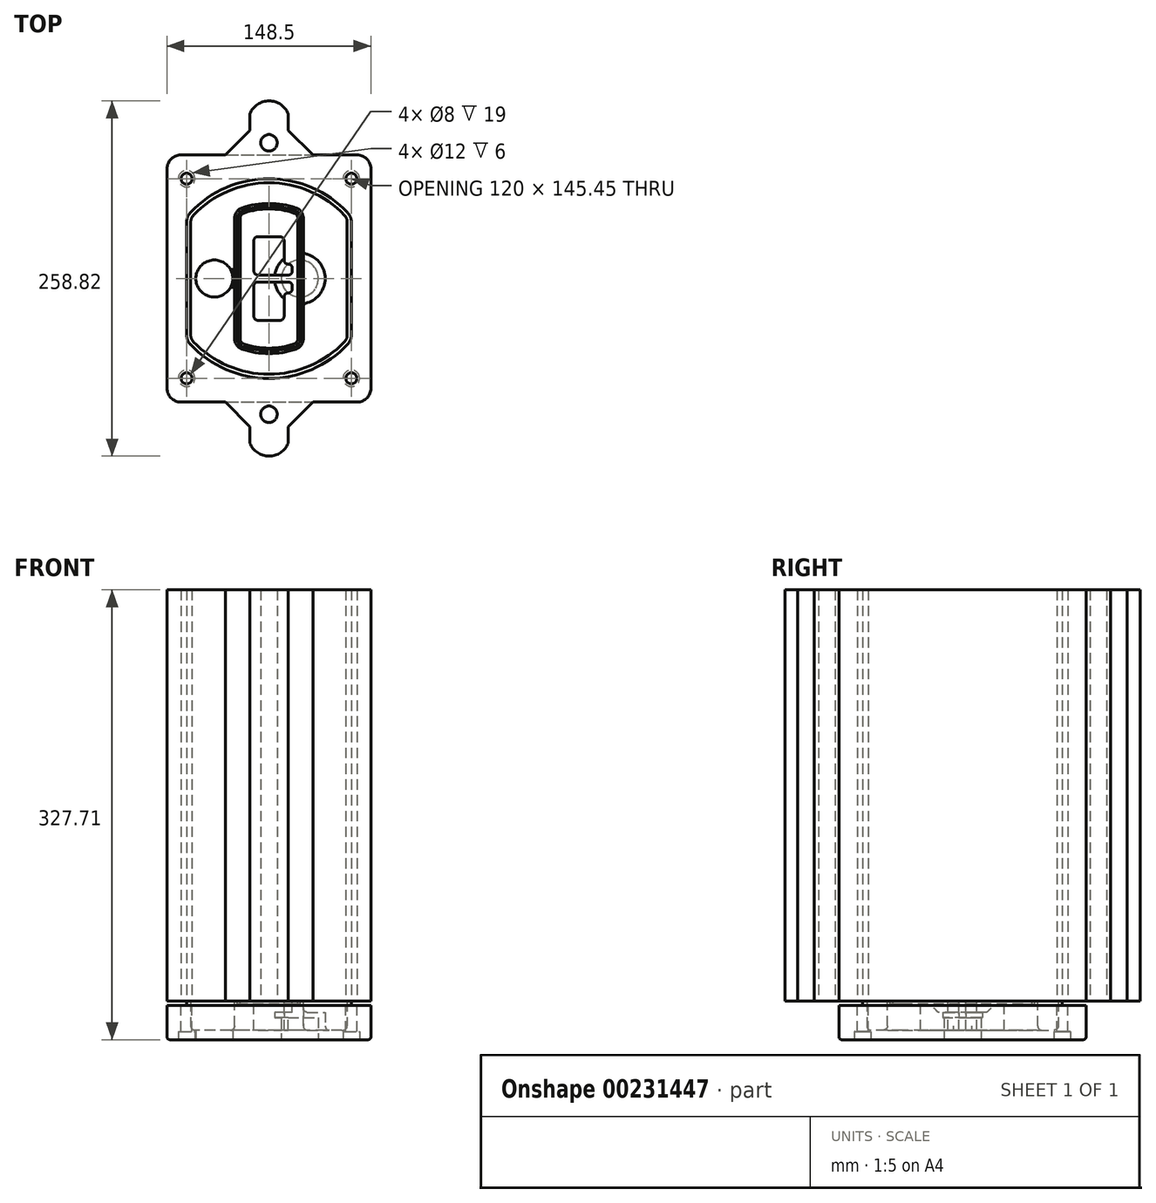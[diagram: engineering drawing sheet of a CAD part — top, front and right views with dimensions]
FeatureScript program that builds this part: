
annotation { "Feature Type Name" : "Feature", "Feature Type Description" : "" }
export const myFeature = defineFeature(function(context is Context, id is Id, definition is map)
    precondition{}
    {
        {
            var Q0;
            Q0=qCreatedBy(makeId("Top.planeOp"),FACE);
            var sketch = newSketch(context, id + "F0", { "sketchPlane" : qUnion([Q0])});
            skPoint(sketch, "E0.rect.middle", {"position": v(0, 0) * mm});
            skLineSegment(sketch, "E1.bottom", {"start": v(-64.25, -90) * mm, "end": v(64.25, -90) * mm});
            skLineSegment(sketch, "E1.top", {"start": v(-64.25, 90) * mm, "end": v(64.25, 90) * mm});
            skLineSegment(sketch, "E1.left", {"start": v(-74.25, -80) * mm, "end": v(-74.25, 80) * mm});
            skLineSegment(sketch, "E1.right", {"start": v(74.25, -80) * mm, "end": v(74.25, 80) * mm});
            skLineSegment(sketch, "E2", {"start": v(-74.25, 90) * mm, "end": v(74.25, -90) * mm, "construction": true});
            skLineSegment(sketch, "E3", {"start": v(74.25, 90) * mm, "end": v(-74.25, -90) * mm, "construction": true});
            skCircle(sketch, "E4", {"center": v(-60, 72.73) * mm, "radius": 4 * mm});
            skCircle(sketch, "E5", {"center": v(60, 72.73) * mm, "radius": 4 * mm});
            skCircle(sketch, "E6", {"center": v(60, -72.73) * mm, "radius": 4 * mm});
            skCircle(sketch, "E7", {"center": v(-60, -72.73) * mm, "radius": 4 * mm});
            skLineSegment(sketch, "E8", {"start": v(-60, 72.73) * mm, "end": v(60, 72.73) * mm, "construction": true});
            skLineSegment(sketch, "E9", {"start": v(60, 72.73) * mm, "end": v(60, -72.73) * mm, "construction": true});
            skLineSegment(sketch, "E10", {"start": v(60, -72.73) * mm, "end": v(-60, -72.73) * mm, "construction": true});
            skLineSegment(sketch, "E11", {"start": v(-60, -72.73) * mm, "end": v(-60, 72.73) * mm, "construction": true});
            skLineSegment(sketch, "E12", {"start": v(-60, 41.18) * mm, "end": v(-60, -41.18) * mm});
            skLineSegment(sketch, "E13", {"start": v(60, 41.18) * mm, "end": v(60, -41.18) * mm});
            skArc(sketch, "E14", {"start": v(57.27, 48.05) * mm, "mid": v(0, 72.73) * mm, "end": v(-57.27, 48.05) * mm});
            skArc(sketch, "E15", {"start": v(-57.27, -48.05) * mm, "mid": v(0, -72.73) * mm, "end": v(57.27, -48.05) * mm});
            skLineSegment(sketch, "E16", {"start": v(-60, 0) * mm, "end": v(60, 0) * mm, "construction": true});
            skPoint(sketch, "E17.visualSharp", {"position": v(-60, -45) * mm});
            skArc(sketch, "E17.filletArc", {"start": v(-60, -41.18) * mm, "mid": v(-59.3, -44.87) * mm, "end": v(-57.27, -48.05) * mm});
            skPoint(sketch, "E18.visualSharp", {"position": v(-60, 45) * mm});
            skArc(sketch, "E18.filletArc", {"start": v(-57.27, 48.05) * mm, "mid": v(-59.3, 44.87) * mm, "end": v(-60, 41.18) * mm});
            skPoint(sketch, "E19.visualSharp", {"position": v(60, 45) * mm});
            skArc(sketch, "E19.filletArc", {"start": v(60, 41.18) * mm, "mid": v(59.3, 44.87) * mm, "end": v(57.27, 48.05) * mm});
            skPoint(sketch, "E20.visualSharp", {"position": v(60, -45) * mm});
            skArc(sketch, "E20.filletArc", {"start": v(57.27, -48.05) * mm, "mid": v(59.3, -44.87) * mm, "end": v(60, -41.18) * mm});
            skPoint(sketch, "E21.visualSharp", {"position": v(-74.25, 90) * mm});
            skArc(sketch, "E21.filletArc", {"start": v(-64.25, 90) * mm, "mid": v(-71.32, 87.07) * mm, "end": v(-74.25, 80) * mm});
            skPoint(sketch, "E22.visualSharp", {"position": v(74.25, 90) * mm});
            skArc(sketch, "E22.filletArc", {"start": v(74.25, 80) * mm, "mid": v(71.32, 87.07) * mm, "end": v(64.25, 90) * mm});
            skPoint(sketch, "E23.visualSharp", {"position": v(74.25, -90) * mm});
            skArc(sketch, "E23.filletArc", {"start": v(64.25, -90) * mm, "mid": v(71.32, -87.07) * mm, "end": v(74.25, -80) * mm});
            skPoint(sketch, "E24.visualSharp", {"position": v(-74.25, -90) * mm});
            skArc(sketch, "E24.filletArc", {"start": v(-74.25, -80) * mm, "mid": v(-71.32, -87.07) * mm, "end": v(-64.25, -90) * mm});
            skArc(sketch, "E25.0", {"start": v(57, 41.18) * mm, "mid": v(56.5, 43.76) * mm, "end": v(55.09, 45.99) * mm});
            skLineSegment(sketch, "E25.1", {"start": v(57, 41.18) * mm, "end": v(57, -41.18) * mm});
            skArc(sketch, "E25.2", {"start": v(55.09, -45.99) * mm, "mid": v(56.5, -43.76) * mm, "end": v(57, -41.18) * mm});
            skArc(sketch, "E25.3", {"start": v(-55.09, -45.99) * mm, "mid": v(0, -69.73) * mm, "end": v(55.09, -45.99) * mm});
            skArc(sketch, "E25.4", {"start": v(-57, -41.18) * mm, "mid": v(-56.5, -43.76) * mm, "end": v(-55.09, -45.99) * mm});
            skArc(sketch, "E25.5", {"start": v(55.09, 45.99) * mm, "mid": v(0, 69.73) * mm, "end": v(-55.09, 45.99) * mm});
            skLineSegment(sketch, "E25.6", {"start": v(-57, 41.18) * mm, "end": v(-57, -41.18) * mm});
            skArc(sketch, "E25.7", {"start": v(-55.09, 45.99) * mm, "mid": v(-56.5, 43.76) * mm, "end": v(-57, 41.18) * mm});
            skArc(sketch, "E26.0", {"start": v(-60.18, 50.8) * mm, "mid": v(-63, 46.35) * mm, "end": v(-64, 41.18) * mm});
            skArc(sketch, "E26.1", {"start": v(60.18, 50.8) * mm, "mid": v(0, 76.73) * mm, "end": v(-60.18, 50.8) * mm});
            skArc(sketch, "E26.2", {"start": v(64, 41.18) * mm, "mid": v(63, 46.35) * mm, "end": v(60.18, 50.8) * mm});
            skLineSegment(sketch, "E26.3", {"start": v(64, 41.18) * mm, "end": v(64, -41.18) * mm});
            skArc(sketch, "E26.4", {"start": v(60.18, -50.8) * mm, "mid": v(63, -46.35) * mm, "end": v(64, -41.18) * mm});
            skLineSegment(sketch, "E26.5", {"start": v(-64, 41.18) * mm, "end": v(-64, -41.18) * mm});
            skArc(sketch, "E26.6", {"start": v(-60.18, -50.8) * mm, "mid": v(0, -76.73) * mm, "end": v(60.18, -50.8) * mm});
            skArc(sketch, "E26.7", {"start": v(-64, -41.18) * mm, "mid": v(-63, -46.35) * mm, "end": v(-60.18, -50.8) * mm});
            skSolve(sketch);
        }
        {
            var Q0;
            Q0=makeQuery(id+"F0.imprint","IMPRINT",FACE,{"disambiguationData":[TD([[makeQuery(id+"F0.imprint","IMPRINT",EDGE,{"derivedFrom":sQuery(id+"F0.wireOp",EDGE,"E1.bottom")}),1.0]])]});
            var Q1;
            Q1=makeQuery(id+"F0.imprint","IMPRINT",FACE,{"disambiguationData":[TD([[makeQuery(id+"F0.imprint","IMPRINT",EDGE,{"derivedFrom":sQuery(id+"F0.wireOp",EDGE,"E12")}),1.0]])]});
            var Q2;
            Q2=makeQuery(id+"F0.imprint","IMPRINT",FACE,{"disambiguationData":[TD([[makeQuery(id+"F0.imprint","IMPRINT",EDGE,{"derivedFrom":sQuery(id+"F0.wireOp",EDGE,"E25.0")}),1.0]])]});
            var Q3;
            Q3=makeQuery(id+"F0.imprint","IMPRINT",FACE,{"disambiguationData":[TD([[makeQuery(id+"F0.imprint","IMPRINT",EDGE,{"derivedFrom":sQuery(id+"F0.wireOp",EDGE,"E12")}),-1.0]])]});
            extrude(context, id + "F1", {"entities" : qUnion([Q0, Q1, Q2, Q3]), "oppositeDirection" : true, "depth" : 25 * mm});
        }
        {
            var Q0;
            Q0=makeQuery(id+"F0.imprint","IMPRINT",FACE,{"disambiguationData":[TD([[makeQuery(id+"F0.imprint","IMPRINT",EDGE,{"derivedFrom":sQuery(id+"F0.wireOp",EDGE,"E12")}),1.0]])]});
            extrude(context, id + "F2", {"entities" : qUnion([Q0]), "operationType" : NewBodyOperationType.ADD, "depth" : 3 * mm});
        }
        {
            var Q0;
            Q0=makeQuery(id+"F0.imprint","IMPRINT",FACE,{"disambiguationData":[TD([[makeQuery(id+"F0.imprint","IMPRINT",EDGE,{"derivedFrom":sQuery(id+"F0.wireOp",EDGE,"E25.0")}),1.0]])]});
            extrude(context, id + "F3", {"entities" : qUnion([Q0]), "operationType" : NewBodyOperationType.REMOVE, "oppositeDirection" : true, "depth" : 18 * mm});
        }
        {
            var Q0;
            Q0=makeQuery(id+"F2.opExtrude","CAP_FACE",FACE,{"disambiguationData":[OSD([sQuery(id+"F0.wireOp",EDGE,"E12"),sQuery(id+"F0.wireOp",EDGE,"E13"),sQuery(id+"F0.wireOp",EDGE,"E14"),sQuery(id+"F0.wireOp",EDGE,"E15"),sQuery(id+"F0.wireOp",EDGE,"E17.filletArc"),sQuery(id+"F0.wireOp",EDGE,"E18.filletArc"),sQuery(id+"F0.wireOp",EDGE,"E19.filletArc"),sQuery(id+"F0.wireOp",EDGE,"E20.filletArc"),sQuery(id+"F0.wireOp",EDGE,"E25.0"),sQuery(id+"F0.wireOp",EDGE,"E25.1"),sQuery(id+"F0.wireOp",EDGE,"E25.2"),sQuery(id+"F0.wireOp",EDGE,"E25.3"),sQuery(id+"F0.wireOp",EDGE,"E25.4"),sQuery(id+"F0.wireOp",EDGE,"E25.5"),sQuery(id+"F0.wireOp",EDGE,"E25.6"),sQuery(id+"F0.wireOp",EDGE,"E25.7")])],"isStart":false});
            var sketch = newSketch(context, id + "F4", { "sketchPlane" : qUnion([Q0])});
            skArc(sketch, "E27.0", {"start": v(-19.58, -51.49) * mm, "mid": v(0, -54.73) * mm, "end": v(19.58, -51.49) * mm});
            skArc(sketch, "E28.0", {"start": v(19.58, 51.49) * mm, "mid": v(0, 54.73) * mm, "end": v(-19.58, 51.49) * mm});
            skLineSegment(sketch, "E29", {"start": v(-25, 43.91) * mm, "end": v(-25, -43.91) * mm});
            skLineSegment(sketch, "E30", {"start": v(25, 43.91) * mm, "end": v(25, -43.91) * mm});
            skLineSegment(sketch, "E31", {"start": v(-25, 49.35) * mm, "end": v(25, 49.35) * mm, "construction": true});
            skLineSegment(sketch, "E32", {"start": v(-25, -49.35) * mm, "end": v(25, -49.35) * mm, "construction": true});
            skPoint(sketch, "E33.visualSharp", {"position": v(-25, 49.35) * mm});
            skArc(sketch, "E33.filletArc", {"start": v(-19.58, 51.49) * mm, "mid": v(-23.5, 48.57) * mm, "end": v(-25, 43.91) * mm});
            skPoint(sketch, "E34.visualSharp", {"position": v(25, 49.35) * mm});
            skArc(sketch, "E34.filletArc", {"start": v(25, 43.91) * mm, "mid": v(23.5, 48.57) * mm, "end": v(19.58, 51.49) * mm});
            skPoint(sketch, "E35.visualSharp", {"position": v(25, -49.35) * mm});
            skArc(sketch, "E35.filletArc", {"start": v(19.58, -51.49) * mm, "mid": v(23.5, -48.57) * mm, "end": v(25, -43.91) * mm});
            skPoint(sketch, "E36.visualSharp", {"position": v(-25, -49.35) * mm});
            skArc(sketch, "E36.filletArc", {"start": v(-25, -43.91) * mm, "mid": v(-23.5, -48.57) * mm, "end": v(-19.58, -51.49) * mm});
            skArc(sketch, "E37.0", {"start": v(55.09, 45.99) * mm, "mid": v(0, 69.73) * mm, "end": v(-55.09, 45.99) * mm});
            skArc(sketch, "E37.1", {"start": v(-55.09, 45.99) * mm, "mid": v(-56.5, 43.76) * mm, "end": v(-57, 41.18) * mm});
            skLineSegment(sketch, "E37.2", {"start": v(-57, 41.18) * mm, "end": v(-57, -41.18) * mm});
            skArc(sketch, "E37.3", {"start": v(-57, -41.18) * mm, "mid": v(-56.5, -43.76) * mm, "end": v(-55.09, -45.99) * mm});
            skArc(sketch, "E37.4", {"start": v(-55.09, -45.99) * mm, "mid": v(0, -69.73) * mm, "end": v(55.09, -45.99) * mm});
            skArc(sketch, "E37.5", {"start": v(55.09, -45.99) * mm, "mid": v(56.5, -43.76) * mm, "end": v(57, -41.18) * mm});
            skLineSegment(sketch, "E37.6", {"start": v(57, 41.18) * mm, "end": v(57, -41.18) * mm});
            skArc(sketch, "E37.7", {"start": v(57, 41.18) * mm, "mid": v(56.5, 43.76) * mm, "end": v(55.09, 45.99) * mm});
            skLineSegment(sketch, "E38.0", {"start": v(23, 43.91) * mm, "end": v(23, -43.91) * mm});
            skArc(sketch, "E38.1", {"start": v(18.93, -49.6) * mm, "mid": v(21.88, -47.4) * mm, "end": v(23, -43.91) * mm});
            skArc(sketch, "E38.2", {"start": v(-18.93, -49.6) * mm, "mid": v(0, -52.73) * mm, "end": v(18.93, -49.6) * mm});
            skArc(sketch, "E38.3", {"start": v(-23, -43.91) * mm, "mid": v(-21.88, -47.4) * mm, "end": v(-18.93, -49.6) * mm});
            skLineSegment(sketch, "E38.4", {"start": v(-23, 43.91) * mm, "end": v(-23, -43.91) * mm});
            skArc(sketch, "E38.5", {"start": v(23, 43.91) * mm, "mid": v(21.88, 47.4) * mm, "end": v(18.93, 49.6) * mm});
            skArc(sketch, "E38.6", {"start": v(-18.93, 49.6) * mm, "mid": v(-21.88, 47.4) * mm, "end": v(-23, 43.91) * mm});
            skArc(sketch, "E38.7", {"start": v(18.93, 49.6) * mm, "mid": v(0, 52.73) * mm, "end": v(-18.93, 49.6) * mm});
            skArc(sketch, "E39.0", {"start": v(21, 43.91) * mm, "mid": v(20.25, 46.24) * mm, "end": v(18.29, 47.7) * mm});
            skLineSegment(sketch, "E39.1", {"start": v(21, 43.91) * mm, "end": v(21, -43.91) * mm});
            skArc(sketch, "E39.2", {"start": v(18.29, -47.7) * mm, "mid": v(20.25, -46.24) * mm, "end": v(21, -43.91) * mm});
            skArc(sketch, "E39.3", {"start": v(-18.29, -47.7) * mm, "mid": v(0, -50.73) * mm, "end": v(18.29, -47.7) * mm});
            skArc(sketch, "E39.4", {"start": v(-21, -43.91) * mm, "mid": v(-20.25, -46.24) * mm, "end": v(-18.29, -47.7) * mm});
            skArc(sketch, "E39.5", {"start": v(18.29, 47.7) * mm, "mid": v(0, 50.73) * mm, "end": v(-18.29, 47.7) * mm});
            skLineSegment(sketch, "E39.6", {"start": v(-21, 43.91) * mm, "end": v(-21, -43.91) * mm});
            skArc(sketch, "E39.7", {"start": v(-18.29, 47.7) * mm, "mid": v(-20.25, 46.24) * mm, "end": v(-21, 43.91) * mm});
            skLineSegment(sketch, "E40", {"start": v(-25, 0) * mm, "end": v(25, 0) * mm, "construction": true});
            skLineSegment(sketch, "E41", {"start": v(-11, 5.5) * mm, "end": v(-11, 27.5) * mm});
            skLineSegment(sketch, "E42", {"start": v(-8, 30.5) * mm, "end": v(8, 30.5) * mm});
            skLineSegment(sketch, "E43", {"start": v(11, 27.5) * mm, "end": v(11, 13.5) * mm});
            skLineSegment(sketch, "E44", {"start": v(14, 10.5) * mm, "end": v(14, 10.5) * mm});
            skLineSegment(sketch, "E45", {"start": v(17, 7.5) * mm, "end": v(17, 5.5) * mm});
            skLineSegment(sketch, "E46", {"start": v(14, 2.5) * mm, "end": v(-8, 2.5) * mm});
            skPoint(sketch, "E47.visualSharp", {"position": v(-11, 30.5) * mm});
            skArc(sketch, "E47.filletArc", {"start": v(-8, 30.5) * mm, "mid": v(-10.12, 29.62) * mm, "end": v(-11, 27.5) * mm});
            skPoint(sketch, "E48.visualSharp", {"position": v(11, 30.5) * mm});
            skArc(sketch, "E48.filletArc", {"start": v(11, 27.5) * mm, "mid": v(10.12, 29.62) * mm, "end": v(8, 30.5) * mm});
            skPoint(sketch, "E49.visualSharp", {"position": v(11, 10.5) * mm});
            skArc(sketch, "E49.filletArc", {"start": v(11, 13.5) * mm, "mid": v(11.88, 11.38) * mm, "end": v(14, 10.5) * mm});
            skPoint(sketch, "E50.visualSharp", {"position": v(17, 10.5) * mm});
            skArc(sketch, "E50.filletArc", {"start": v(17, 7.5) * mm, "mid": v(16.12, 9.62) * mm, "end": v(14, 10.5) * mm});
            skPoint(sketch, "E51.visualSharp", {"position": v(17, 2.5) * mm});
            skArc(sketch, "E51.filletArc", {"start": v(14, 2.5) * mm, "mid": v(16.12, 3.38) * mm, "end": v(17, 5.5) * mm});
            skPoint(sketch, "E52.visualSharp", {"position": v(-11, 2.5) * mm});
            skArc(sketch, "E52.filletArc", {"start": v(-11, 5.5) * mm, "mid": v(-10.12, 3.38) * mm, "end": v(-8, 2.5) * mm});
            skLineSegment(sketch, "E53.0.MirrorCS", {"start": v(14, -2.5) * mm, "end": v(-8, -2.5) * mm});
            skArc(sketch, "E54.0.MirrorCS", {"start": v(-11, -5.5) * mm, "mid": v(-10.12, -3.38) * mm, "end": v(-8, -2.5) * mm});
            skLineSegment(sketch, "E55.0.MirrorCS", {"start": v(-11, -5.5) * mm, "end": v(-11, -27.5) * mm});
            skArc(sketch, "E56.0.MirrorCS", {"start": v(-8, -30.5) * mm, "mid": v(-10.12, -29.62) * mm, "end": v(-11, -27.5) * mm});
            skLineSegment(sketch, "E57.0.MirrorCS", {"start": v(-8, -30.5) * mm, "end": v(8, -30.5) * mm});
            skArc(sketch, "E58.0.MirrorCS", {"start": v(11, -27.5) * mm, "mid": v(10.12, -29.62) * mm, "end": v(8, -30.5) * mm});
            skLineSegment(sketch, "E59.0.MirrorCS", {"start": v(11, -27.5) * mm, "end": v(11, -13.5) * mm});
            skArc(sketch, "E60.0.MirrorCS", {"start": v(11, -13.5) * mm, "mid": v(11.88, -11.38) * mm, "end": v(14, -10.5) * mm});
            skArc(sketch, "E61.0.MirrorCS", {"start": v(17, -7.5) * mm, "mid": v(16.12, -9.62) * mm, "end": v(14, -10.5) * mm});
            skLineSegment(sketch, "E62.0.MirrorCS", {"start": v(17, -7.5) * mm, "end": v(17, -5.5) * mm});
            skArc(sketch, "E63.0.MirrorCS", {"start": v(14, -2.5) * mm, "mid": v(16.12, -3.38) * mm, "end": v(17, -5.5) * mm});
            skSolve(sketch);
        }
        {
            var Q0;
            Q0=makeQuery(id+"F4.imprint","IMPRINT",FACE,{"disambiguationData":[TD([[makeQuery(id+"F4.imprint","IMPRINT",EDGE,{"derivedFrom":sQuery(id+"F4.wireOp",EDGE,"E27.0")}),1.0]])]});
            var Q1;
            Q1=makeQuery(id+"F4.imprint","IMPRINT",FACE,{"disambiguationData":[TD([[makeQuery(id+"F4.imprint","IMPRINT",EDGE,{"derivedFrom":sQuery(id+"F4.wireOp",EDGE,"E38.0")}),-1.0]])]});
            var Q2;
            Q2=makeQuery(id+"F4.imprint","IMPRINT",FACE,{"disambiguationData":[TD([[makeQuery(id+"F4.imprint","IMPRINT",EDGE,{"derivedFrom":sQuery(id+"F4.wireOp",EDGE,"E39.0")}),1.0]])]});
            extrude(context, id + "F5", {"entities" : qUnion([Q0, Q1, Q2]), "operationType" : NewBodyOperationType.ADD, "endBound" : BoundingType.UP_TO_NEXT, "oppositeDirection" : true, "depth" : 25 * mm});
        }
        {
            var Q0;
            Q0=makeQuery(id+"F4.imprint","IMPRINT",FACE,{"disambiguationData":[TD([[makeQuery(id+"F4.imprint","IMPRINT",EDGE,{"derivedFrom":sQuery(id+"F4.wireOp",EDGE,"E38.0")}),-1.0]])]});
            extrude(context, id + "F6", {"entities" : qUnion([Q0]), "operationType" : NewBodyOperationType.REMOVE, "oppositeDirection" : true, "depth" : 2 * mm});
        }
        {
            var Q0;
            Q0=makeQuery(id+"F1.opExtrude","CAP_FACE",FACE,{"disambiguationData":[OSD([sQuery(id+"F0.wireOp",EDGE,"E1.bottom"),sQuery(id+"F0.wireOp",EDGE,"E1.top"),sQuery(id+"F0.wireOp",EDGE,"E1.left"),sQuery(id+"F0.wireOp",EDGE,"E1.right"),sQuery(id+"F0.wireOp",EDGE,"E4"),sQuery(id+"F0.wireOp",EDGE,"E5"),sQuery(id+"F0.wireOp",EDGE,"E6"),sQuery(id+"F0.wireOp",EDGE,"E7"),sQuery(id+"F0.wireOp",EDGE,"E21.filletArc"),sQuery(id+"F0.wireOp",EDGE,"E22.filletArc"),sQuery(id+"F0.wireOp",EDGE,"E23.filletArc"),sQuery(id+"F0.wireOp",EDGE,"E24.filletArc")])],"isStart":false});
            var sketch = newSketch(context, id + "F7", { "sketchPlane" : qUnion([Q0])});
            skCircle(sketch, "E64", {"center": v(22.5, 0) * mm, "radius": 13.47 * mm});
            skCircle(sketch, "E65", {"center": v(-39.81, 0) * mm, "radius": 13.47 * mm});
            skLineSegment(sketch, "E66", {"start": v(74.25, 0) * mm, "end": v(-74.25, 0) * mm});
            skCircle(sketch, "E67", {"center": v(22.5, 0) * mm, "radius": 18.47 * mm});
            skCircle(sketch, "E68", {"center": v(60, -72.73) * mm, "radius": 6 * mm});
            skCircle(sketch, "E69", {"center": v(-60, -72.73) * mm, "radius": 6 * mm});
            skCircle(sketch, "E70", {"center": v(-60, 72.73) * mm, "radius": 6 * mm});
            skCircle(sketch, "E71", {"center": v(60, 72.73) * mm, "radius": 6 * mm});
            skSolve(sketch);
        }
        {
            var Q0;
            {var subQ1=sQuery(id+"F7.wireOp",EDGE,"E66");var subQ4=sQuery(id+"F7.wireOp",EDGE,"E64");var subQ6=makeQuery(id+"F7.imprint","INTERSECT",VERTEX,{"disambiguationData":[OD(0.0)],"derivedFrom":[subQ4,subQ1]});Q0=makeQuery(id+"F7.imprint","IMPRINT",FACE,{"disambiguationData":[TD([[makeQuery(id+"F7.imprint","IMPRINT",EDGE,{"disambiguationData":[TD([[subQ6,-1.0]])],"derivedFrom":subQ4}),-1.0]])]});}
            var Q1;
            {var subQ0=sQuery(id+"F7.wireOp",EDGE,"E66");var subQ1=sQuery(id+"F7.wireOp",EDGE,"E64");var subQ3=makeQuery(id+"F7.imprint","INTERSECT",VERTEX,{"disambiguationData":[OD(0.0)],"derivedFrom":[subQ1,subQ0]});Q1=makeQuery(id+"F7.imprint","IMPRINT",FACE,{"disambiguationData":[TD([[makeQuery(id+"F7.imprint","IMPRINT",EDGE,{"disambiguationData":[TD([[subQ3,-1.0]])],"derivedFrom":subQ1}),1.0]])]});}
            var Q2;
            {var subQ0=sQuery(id+"F7.wireOp",EDGE,"E66");var subQ1=sQuery(id+"F7.wireOp",EDGE,"E64");var subQ3=makeQuery(id+"F7.imprint","INTERSECT",VERTEX,{"disambiguationData":[OD(0.0)],"derivedFrom":[subQ1,subQ0]});Q2=makeQuery(id+"F7.imprint","IMPRINT",FACE,{"disambiguationData":[TD([[makeQuery(id+"F7.imprint","IMPRINT",EDGE,{"disambiguationData":[TD([[subQ3,1.0]])],"derivedFrom":subQ1}),1.0]])]});}
            var Q3;
            {var subQ1=sQuery(id+"F7.wireOp",EDGE,"E66");var subQ4=sQuery(id+"F7.wireOp",EDGE,"E64");var subQ6=makeQuery(id+"F7.imprint","INTERSECT",VERTEX,{"disambiguationData":[OD(0.0)],"derivedFrom":[subQ4,subQ1]});Q3=makeQuery(id+"F7.imprint","IMPRINT",FACE,{"disambiguationData":[TD([[makeQuery(id+"F7.imprint","IMPRINT",EDGE,{"disambiguationData":[TD([[subQ6,1.0]])],"derivedFrom":subQ4}),-1.0]])]});}
            extrude(context, id + "F8", {"entities" : qUnion([Q0, Q1, Q2, Q3]), "operationType" : NewBodyOperationType.ADD, "oppositeDirection" : true, "depth" : 20 * mm});
        }
        {
            var Q0;
            {var subQ0=sQuery(id+"F7.wireOp",EDGE,"E66");var subQ1=sQuery(id+"F7.wireOp",EDGE,"E64");var subQ3=makeQuery(id+"F7.imprint","INTERSECT",VERTEX,{"disambiguationData":[OD(0.0)],"derivedFrom":[subQ1,subQ0]});Q0=makeQuery(id+"F7.imprint","IMPRINT",FACE,{"disambiguationData":[TD([[makeQuery(id+"F7.imprint","IMPRINT",EDGE,{"disambiguationData":[TD([[subQ3,-1.0]])],"derivedFrom":subQ1}),1.0]])]});}
            var Q1;
            {var subQ0=sQuery(id+"F7.wireOp",EDGE,"E66");var subQ1=sQuery(id+"F7.wireOp",EDGE,"E64");var subQ3=makeQuery(id+"F7.imprint","INTERSECT",VERTEX,{"disambiguationData":[OD(0.0)],"derivedFrom":[subQ1,subQ0]});Q1=makeQuery(id+"F7.imprint","IMPRINT",FACE,{"disambiguationData":[TD([[makeQuery(id+"F7.imprint","IMPRINT",EDGE,{"disambiguationData":[TD([[subQ3,1.0]])],"derivedFrom":subQ1}),1.0]])]});}
            extrude(context, id + "F9", {"entities" : qUnion([Q0, Q1]), "operationType" : NewBodyOperationType.REMOVE, "oppositeDirection" : true, "depth" : 16 * mm});
        }
        {
            var Q0;
            {var subQ0=sQuery(id+"F7.wireOp",EDGE,"E66");var subQ1=sQuery(id+"F7.wireOp",EDGE,"E65");var subQ3=makeQuery(id+"F7.imprint","INTERSECT",VERTEX,{"disambiguationData":[OD(0.0)],"derivedFrom":[subQ1,subQ0]});Q0=makeQuery(id+"F7.imprint","IMPRINT",FACE,{"disambiguationData":[TD([[makeQuery(id+"F7.imprint","IMPRINT",EDGE,{"disambiguationData":[TD([[subQ3,-1.0]])],"derivedFrom":subQ1}),1.0]])]});}
            var Q1;
            {var subQ0=sQuery(id+"F7.wireOp",EDGE,"E66");var subQ1=sQuery(id+"F7.wireOp",EDGE,"E65");var subQ3=makeQuery(id+"F7.imprint","INTERSECT",VERTEX,{"disambiguationData":[OD(0.0)],"derivedFrom":[subQ1,subQ0]});Q1=makeQuery(id+"F7.imprint","IMPRINT",FACE,{"disambiguationData":[TD([[makeQuery(id+"F7.imprint","IMPRINT",EDGE,{"disambiguationData":[TD([[subQ3,1.0]])],"derivedFrom":subQ1}),1.0]])]});}
            extrude(context, id + "F10", {"entities" : qUnion([Q0, Q1]), "operationType" : NewBodyOperationType.REMOVE, "oppositeDirection" : true, "depth" : 25 * mm});
        }
        {
            var Q0;
            Q0=makeQuery(id+"F7.imprint","IMPRINT",FACE,{"disambiguationData":[TD([[makeQuery(id+"F7.imprint","IMPRINT",EDGE,{"derivedFrom":sQuery(id+"F7.wireOp",EDGE,"E68")}),1.0]])]});
            var Q1;
            Q1=makeQuery(id+"F7.imprint","IMPRINT",FACE,{"disambiguationData":[TD([[makeQuery(id+"F7.imprint","IMPRINT",EDGE,{"derivedFrom":makeQuery(id+"F1.opExtrude","CAP_EDGE",EDGE,{"disambiguationData":[OSD([sQuery(id+"F0.wireOp",EDGE,"E5")])],"isStart":false})}),-1.0]])]});
            var Q2;
            Q2=makeQuery(id+"F7.imprint","IMPRINT",FACE,{"disambiguationData":[TD([[makeQuery(id+"F7.imprint","IMPRINT",EDGE,{"derivedFrom":sQuery(id+"F7.wireOp",EDGE,"E69")}),1.0]])]});
            var Q3;
            Q3=makeQuery(id+"F7.imprint","IMPRINT",FACE,{"disambiguationData":[TD([[makeQuery(id+"F7.imprint","IMPRINT",EDGE,{"derivedFrom":makeQuery(id+"F1.opExtrude","CAP_EDGE",EDGE,{"disambiguationData":[OSD([sQuery(id+"F0.wireOp",EDGE,"E4")])],"isStart":false})}),-1.0]])]});
            var Q4;
            Q4=makeQuery(id+"F7.imprint","IMPRINT",FACE,{"disambiguationData":[TD([[makeQuery(id+"F7.imprint","IMPRINT",EDGE,{"derivedFrom":sQuery(id+"F7.wireOp",EDGE,"E70")}),1.0]])]});
            var Q5;
            Q5=makeQuery(id+"F7.imprint","IMPRINT",FACE,{"disambiguationData":[TD([[makeQuery(id+"F7.imprint","IMPRINT",EDGE,{"derivedFrom":makeQuery(id+"F1.opExtrude","CAP_EDGE",EDGE,{"disambiguationData":[OSD([sQuery(id+"F0.wireOp",EDGE,"E7")])],"isStart":false})}),-1.0]])]});
            var Q6;
            Q6=makeQuery(id+"F7.imprint","IMPRINT",FACE,{"disambiguationData":[TD([[makeQuery(id+"F7.imprint","IMPRINT",EDGE,{"derivedFrom":sQuery(id+"F7.wireOp",EDGE,"E71")}),1.0]])]});
            var Q7;
            Q7=makeQuery(id+"F7.imprint","IMPRINT",FACE,{"disambiguationData":[TD([[makeQuery(id+"F7.imprint","IMPRINT",EDGE,{"derivedFrom":makeQuery(id+"F1.opExtrude","CAP_EDGE",EDGE,{"disambiguationData":[OSD([sQuery(id+"F0.wireOp",EDGE,"E6")])],"isStart":false})}),-1.0]])]});
            extrude(context, id + "F11", {"entities" : qUnion([Q0, Q1, Q2, Q3, Q4, Q5, Q6, Q7]), "operationType" : NewBodyOperationType.REMOVE, "oppositeDirection" : true, "depth" : 6 * mm});
        }
        {
            var Q0;
            Q0=makeQuery(id+"F9.boolean.opBoolean","COPY",FACE,{"derivedFrom":makeQuery(id+"F9.opExtrude","CAP_FACE",FACE,{"disambiguationData":[OSD([sQuery(id+"F7.wireOp",EDGE,"E64")])],"isStart":false})});
            var sketch = newSketch(context, id + "F12", { "sketchPlane" : qUnion([Q0])});
            skArc(sketch, "E72.0", {"start": v(11, 14.45) * mm, "mid": v(6.45, 9.13) * mm, "end": v(4.2, 2.5) * mm});
            skArc(sketch, "E72.1", {"start": v(4.2, -2.5) * mm, "mid": v(6.45, -9.13) * mm, "end": v(11, -14.45) * mm});
            skLineSegment(sketch, "E73", {"start": v(4.2, -2.5) * mm, "end": v(14, -2.5) * mm});
            skLineSegment(sketch, "E74.0", {"start": v(14, 2.5) * mm, "end": v(4.2, 2.5) * mm});
            skArc(sketch, "E74.1", {"start": v(14, 2.5) * mm, "mid": v(16.12, 3.38) * mm, "end": v(17, 5.5) * mm});
            skLineSegment(sketch, "E74.2", {"start": v(17, 7.5) * mm, "end": v(17, 5.5) * mm});
            skArc(sketch, "E74.3", {"start": v(17, 7.5) * mm, "mid": v(16.12, 9.62) * mm, "end": v(14, 10.5) * mm});
            skArc(sketch, "E74.4", {"start": v(11, 13.5) * mm, "mid": v(11.88, 11.38) * mm, "end": v(14, 10.5) * mm});
            skLineSegment(sketch, "E74.5", {"start": v(11, 14.45) * mm, "end": v(11, 13.5) * mm});
            skLineSegment(sketch, "E74.7", {"start": v(14, -2.5) * mm, "end": v(4.2, -2.5) * mm});
            skArc(sketch, "E74.8", {"start": v(14, -2.5) * mm, "mid": v(16.12, -3.38) * mm, "end": v(17, -5.5) * mm});
            skLineSegment(sketch, "E74.9", {"start": v(17, -7.5) * mm, "end": v(17, -5.5) * mm});
            skArc(sketch, "E74.10", {"start": v(17, -7.5) * mm, "mid": v(16.12, -9.62) * mm, "end": v(14, -10.5) * mm});
            skArc(sketch, "E74.11", {"start": v(11, -13.5) * mm, "mid": v(11.88, -11.38) * mm, "end": v(14, -10.5) * mm});
            skLineSegment(sketch, "E74.12", {"start": v(11, -14.45) * mm, "end": v(11, -13.5) * mm});
            skPoint(sketch, "E75.orphan", {"position": v(11, -27.5) * mm});
            skPoint(sketch, "E76.orphan", {"position": v(-8, -2.5) * mm});
            skPoint(sketch, "E77.orphan", {"position": v(-8, 2.5) * mm});
            skPoint(sketch, "E78.orphan", {"position": v(11, 27.5) * mm});
            skSolve(sketch);
        }
        {
            var Q0;
            {var subQ7=sQuery(id+"F12.wireOp",EDGE,"E72.0");var subQ14=sQuery(id+"F12.wireOp",EDGE,"E72.1");var subQ16=sQuery(id+"F12.wireOp",EDGE,"E74.1");var subQ18=sQuery(id+"F12.wireOp",EDGE,"E74.8");Q0=qUnion([makeQuery(id+"F12.imprint","IMPRINT",FACE,{"disambiguationData":[TD([[makeQuery(id+"F12.imprint","IMPRINT",EDGE,{"derivedFrom":subQ7}),1.0]])]}),makeQuery(id+"F12.imprint","IMPRINT",FACE,{"disambiguationData":[TD([[makeQuery(id+"F12.imprint","IMPRINT",EDGE,{"derivedFrom":subQ14}),1.0]])]}),makeQuery(id+"F12.imprint","IMPRINT",FACE,{"disambiguationData":[TD([[makeQuery(id+"F12.imprint","IMPRINT",EDGE,{"derivedFrom":subQ16}),1.0]])]}),makeQuery(id+"F12.imprint","IMPRINT",FACE,{"disambiguationData":[TD([[makeQuery(id+"F12.imprint","IMPRINT",EDGE,{"derivedFrom":subQ18}),-1.0]])]})]);}
            var Q1;
            Q1=makeQuery(id+"F5.boolean.opBoolean","SPLIT",FACE,{"disambiguationData":[TD([makeQuery(id+"F5.opExtrude","SWEPT_FACE",FACE,{"disambiguationData":[OSD([sQuery(id+"F4.wireOp",EDGE,"E41")])]})])],"derivedFrom":makeQuery(id+"F3.boolean.opBoolean","COPY",FACE,{"derivedFrom":makeQuery(id+"F3.opExtrude","CAP_FACE",FACE,{"disambiguationData":[OSD([sQuery(id+"F0.wireOp",EDGE,"E25.0"),sQuery(id+"F0.wireOp",EDGE,"E25.1"),sQuery(id+"F0.wireOp",EDGE,"E25.2"),sQuery(id+"F0.wireOp",EDGE,"E25.3"),sQuery(id+"F0.wireOp",EDGE,"E25.4"),sQuery(id+"F0.wireOp",EDGE,"E25.5"),sQuery(id+"F0.wireOp",EDGE,"E25.6"),sQuery(id+"F0.wireOp",EDGE,"E25.7")])],"isStart":false})})});
            extrude(context, id + "F13", {"entities" : qUnion([Q0]), "operationType" : NewBodyOperationType.REMOVE, "endBound" : BoundingType.UP_TO_SURFACE, "endBoundEntityFace" : qUnion([Q1]), "depth" : 25 * mm});
        }
        {
            var Q0;
            Q0=makeQuery(id+"F3.boolean.opBoolean","COPY",EDGE,{"derivedFrom":makeQuery(id+"F3.opExtrude","CAP_EDGE",EDGE,{"disambiguationData":[OSD([sQuery(id+"F0.wireOp",EDGE,"E25.6")])],"isStart":false})});
            var Q1;
            Q1=makeQuery(id+"F8.boolean.opBoolean","INTERSECT",EDGE,{"derivedFrom":[makeQuery(id+"F5.opExtrude","SWEPT_FACE",FACE,{"disambiguationData":[OSD([sQuery(id+"F4.wireOp",EDGE,"E30")])]}),makeQuery(id+"F8.opExtrude","CAP_FACE",FACE,{"disambiguationData":[OSD([sQuery(id+"F7.wireOp",EDGE,"E67")])],"isStart":false})]});
            var Q2;
            Q2=makeQuery(id+"F8.boolean.opBoolean","INTERSECT",EDGE,{"disambiguationData":[OD(1.0)],"derivedFrom":[makeQuery(id+"F5.opExtrude","SWEPT_FACE",FACE,{"disambiguationData":[OSD([sQuery(id+"F4.wireOp",EDGE,"E30")])]}),makeQuery(id+"F8.opExtrude","SWEPT_FACE",FACE,{"disambiguationData":[OSD([sQuery(id+"F7.wireOp",EDGE,"E67")])]})]});
            var Q3;
            {var subQ0=sQuery(id+"F4.wireOp",EDGE,"E30");Q3=makeQuery(id+"F8.boolean.opBoolean","SPLIT",EDGE,{"disambiguationData":[TD([makeQuery(id+"F5.opExtrude","SWEPT_FACE",FACE,{"disambiguationData":[OSD([sQuery(id+"F4.wireOp",EDGE,"E35.filletArc")])]})])],"derivedFrom":makeQuery(id+"F5.opExtrude","CAP_EDGE",EDGE,{"disambiguationData":[OSD([subQ0])],"isStart":false})});}
            var Q4;
            {var subQ0=sQuery(id+"F0.wireOp",EDGE,"E25.7");var subQ1=sQuery(id+"F0.wireOp",EDGE,"E25.1");var subQ2=sQuery(id+"F0.wireOp",EDGE,"E25.6");var subQ3=sQuery(id+"F0.wireOp",EDGE,"E25.5");var subQ4=sQuery(id+"F0.wireOp",EDGE,"E25.4");var subQ5=sQuery(id+"F0.wireOp",EDGE,"E25.0");var subQ6=sQuery(id+"F0.wireOp",EDGE,"E25.2");var subQ7=sQuery(id+"F0.wireOp",EDGE,"E25.3");Q4=makeQuery(id+"F8.boolean.opBoolean","INTERSECT",EDGE,{"derivedFrom":[makeQuery(id+"F5.boolean.opBoolean","SPLIT",FACE,{"disambiguationData":[TD([makeQuery(id+"F2.opExtrude","SWEPT_FACE",FACE,{"disambiguationData":[OSD([subQ5])]})])],"derivedFrom":makeQuery(id+"F3.boolean.opBoolean","COPY",FACE,{"derivedFrom":makeQuery(id+"F3.opExtrude","CAP_FACE",FACE,{"disambiguationData":[OSD([subQ5,subQ1,subQ6,subQ7,subQ4,subQ3,subQ2,subQ0])],"isStart":false})})}),makeQuery(id+"F8.opExtrude","SWEPT_FACE",FACE,{"disambiguationData":[OSD([sQuery(id+"F7.wireOp",EDGE,"E67")])]})]});}
            var Q5;
            Q5=makeQuery(id+"F8.boolean.opBoolean","INTERSECT",EDGE,{"disambiguationData":[OD(0.0)],"derivedFrom":[makeQuery(id+"F5.opExtrude","SWEPT_FACE",FACE,{"disambiguationData":[OSD([sQuery(id+"F4.wireOp",EDGE,"E30")])]}),makeQuery(id+"F8.opExtrude","SWEPT_FACE",FACE,{"disambiguationData":[OSD([sQuery(id+"F7.wireOp",EDGE,"E67")])]})]});
            fillet(context, id + "F14", {"entities" : qUnion([Q0, Q1, Q2, Q3, Q4, Q5]), "radius" : 3 * mm, "tangentPropagation" : true, "allowEdgeOverflow" : false});
        }
        {
            var Q0;
            Q0=makeQuery(id+"F1.opExtrude","CAP_EDGE",EDGE,{"disambiguationData":[OSD([sQuery(id+"F0.wireOp",EDGE,"E1.bottom")])],"isStart":false});
            fillet(context, id + "F15", {"entities" : qUnion([Q0]), "radius" : 2 * mm, "tangentPropagation" : true, "allowEdgeOverflow" : false});
        }
        {
            var Q0;
            Q0=makeQuery(id+"F2.opExtrude","CAP_FACE",FACE,{"disambiguationData":[OSD([sQuery(id+"F0.wireOp",EDGE,"E12"),sQuery(id+"F0.wireOp",EDGE,"E13"),sQuery(id+"F0.wireOp",EDGE,"E14"),sQuery(id+"F0.wireOp",EDGE,"E15"),sQuery(id+"F0.wireOp",EDGE,"E17.filletArc"),sQuery(id+"F0.wireOp",EDGE,"E18.filletArc"),sQuery(id+"F0.wireOp",EDGE,"E19.filletArc"),sQuery(id+"F0.wireOp",EDGE,"E20.filletArc"),sQuery(id+"F0.wireOp",EDGE,"E25.0"),sQuery(id+"F0.wireOp",EDGE,"E25.1"),sQuery(id+"F0.wireOp",EDGE,"E25.2"),sQuery(id+"F0.wireOp",EDGE,"E25.3"),sQuery(id+"F0.wireOp",EDGE,"E25.4"),sQuery(id+"F0.wireOp",EDGE,"E25.5"),sQuery(id+"F0.wireOp",EDGE,"E25.6"),sQuery(id+"F0.wireOp",EDGE,"E25.7")])],"isStart":false});
            var sketch = newSketch(context, id + "F16", { "sketchPlane" : qUnion([Q0])});
            skLineSegment(sketch, "E79.0", {"start": v(-64.25, 90) * mm, "end": v(64.25, 90) * mm});
            skArc(sketch, "E79.1", {"start": v(57.27, 48.05) * mm, "mid": v(0, 72.73) * mm, "end": v(-57.27, 48.05) * mm});
            skLineSegment(sketch, "E79.2", {"start": v(-60, 41.18) * mm, "end": v(-60, -41.18) * mm});
            skArc(sketch, "E79.3", {"start": v(-57.27, 48.05) * mm, "mid": v(-59.3, 44.87) * mm, "end": v(-60, 41.18) * mm});
            skArc(sketch, "E79.4", {"start": v(-60, -41.18) * mm, "mid": v(-59.3, -44.87) * mm, "end": v(-57.27, -48.05) * mm});
            skArc(sketch, "E79.5", {"start": v(-57.27, -48.05) * mm, "mid": v(0, -72.73) * mm, "end": v(57.27, -48.05) * mm});
            skArc(sketch, "E79.6", {"start": v(57.27, -48.05) * mm, "mid": v(59.3, -44.87) * mm, "end": v(60, -41.18) * mm});
            skLineSegment(sketch, "E79.7", {"start": v(60, 41.18) * mm, "end": v(60, -41.18) * mm});
            skArc(sketch, "E79.8", {"start": v(60, 41.18) * mm, "mid": v(59.3, 44.87) * mm, "end": v(57.27, 48.05) * mm});
            skArc(sketch, "E79.9", {"start": v(74.25, 80) * mm, "mid": v(71.32, 87.07) * mm, "end": v(64.25, 90) * mm});
            skLineSegment(sketch, "E79.10", {"start": v(74.25, -80) * mm, "end": v(74.25, 80) * mm});
            skArc(sketch, "E79.11", {"start": v(64.25, -90) * mm, "mid": v(71.32, -87.07) * mm, "end": v(74.25, -80) * mm});
            skLineSegment(sketch, "E79.12", {"start": v(-64.25, -90) * mm, "end": v(64.25, -90) * mm});
            skArc(sketch, "E79.13", {"start": v(-74.25, -80) * mm, "mid": v(-71.32, -87.07) * mm, "end": v(-64.25, -90) * mm});
            skLineSegment(sketch, "E79.14", {"start": v(-74.25, -80) * mm, "end": v(-74.25, 80) * mm});
            skArc(sketch, "E79.15", {"start": v(-64.25, 90) * mm, "mid": v(-71.32, 87.07) * mm, "end": v(-74.25, 80) * mm});
            skCircle(sketch, "E79.16", {"center": v(-60, 72.73) * mm, "radius": 4 * mm});
            skCircle(sketch, "E79.17", {"center": v(60, 72.73) * mm, "radius": 4 * mm});
            skCircle(sketch, "E79.18", {"center": v(60, -72.73) * mm, "radius": 4 * mm});
            skCircle(sketch, "E79.19", {"center": v(-60, -72.73) * mm, "radius": 4 * mm});
            skLineSegment(sketch, "E80.0.0", {"start": v(64.25, 90) * mm, "end": v(-64.25, 90) * mm});
            skLineSegment(sketch, "E80.0.2", {"start": v(-74.25, 80) * mm, "end": v(-74.25, -80) * mm});
            skLineSegment(sketch, "E81.0", {"start": v(-64.25, 88) * mm, "end": v(-64.25, 90) * mm});
            skLineSegment(sketch, "E81.1", {"start": v(-64.25, 88) * mm, "end": v(64.25, 88) * mm});
            skLineSegment(sketch, "E82", {"start": v(-13.85, 108) * mm, "end": v(-13.85, 120) * mm});
            skLineSegment(sketch, "E83", {"start": v(14, 108) * mm, "end": v(14, 120) * mm});
            skArc(sketch, "E84", {"start": v(14, 120) * mm, "mid": v(0.07, 129.4) * mm, "end": v(-13.85, 120) * mm});
            skCircle(sketch, "E85", {"center": v(0, 98.89) * mm, "radius": 6 * mm});
            skLineSegment(sketch, "E86", {"start": v(0, 98.89) * mm, "end": v(0, 90) * mm, "construction": true});
            skLineSegment(sketch, "E87", {"start": v(-13.85, 108) * mm, "end": v(-31.85, 90) * mm});
            skLineSegment(sketch, "E88", {"start": v(14, 108) * mm, "end": v(32, 90) * mm});
            skLineSegment(sketch, "E89", {"start": v(-74.25, 0) * mm, "end": v(74.25, 0) * mm, "construction": true});
            skArc(sketch, "E90.MirrorCS", {"start": v(14, -120) * mm, "mid": v(0.07, -129.4) * mm, "end": v(-13.85, -120) * mm});
            skCircle(sketch, "E91.MirrorC", {"center": v(0, -98.89) * mm, "radius": 6 * mm});
            skLineSegment(sketch, "E92.MirrorCS", {"start": v(-13.85, -108) * mm, "end": v(-31.85, -90) * mm});
            skLineSegment(sketch, "E93.MirrorCS", {"start": v(14, -108) * mm, "end": v(32, -90) * mm});
            skLineSegment(sketch, "E94.MirrorCS", {"start": v(14, -108) * mm, "end": v(14, -120) * mm});
            skLineSegment(sketch, "E95.MirrorCS", {"start": v(-13.85, -108) * mm, "end": v(-13.85, -120) * mm});
            skLineSegment(sketch, "E96.MirrorCS", {"start": v(0, -98.89) * mm, "end": v(0, -90) * mm, "construction": true});
            skSolve(sketch);
        }
        {
            var Q0;
            Q0 = qSketchRegion(id + "F16", true);
            extrude(context, id + "F17", {"entities" : qUnion([Q0]), "operationType" : NewBodyOperationType.ADD, "endBound" : BoundingType.THROUGH_ALL, "depth" : 25 * mm});
        }
    });
